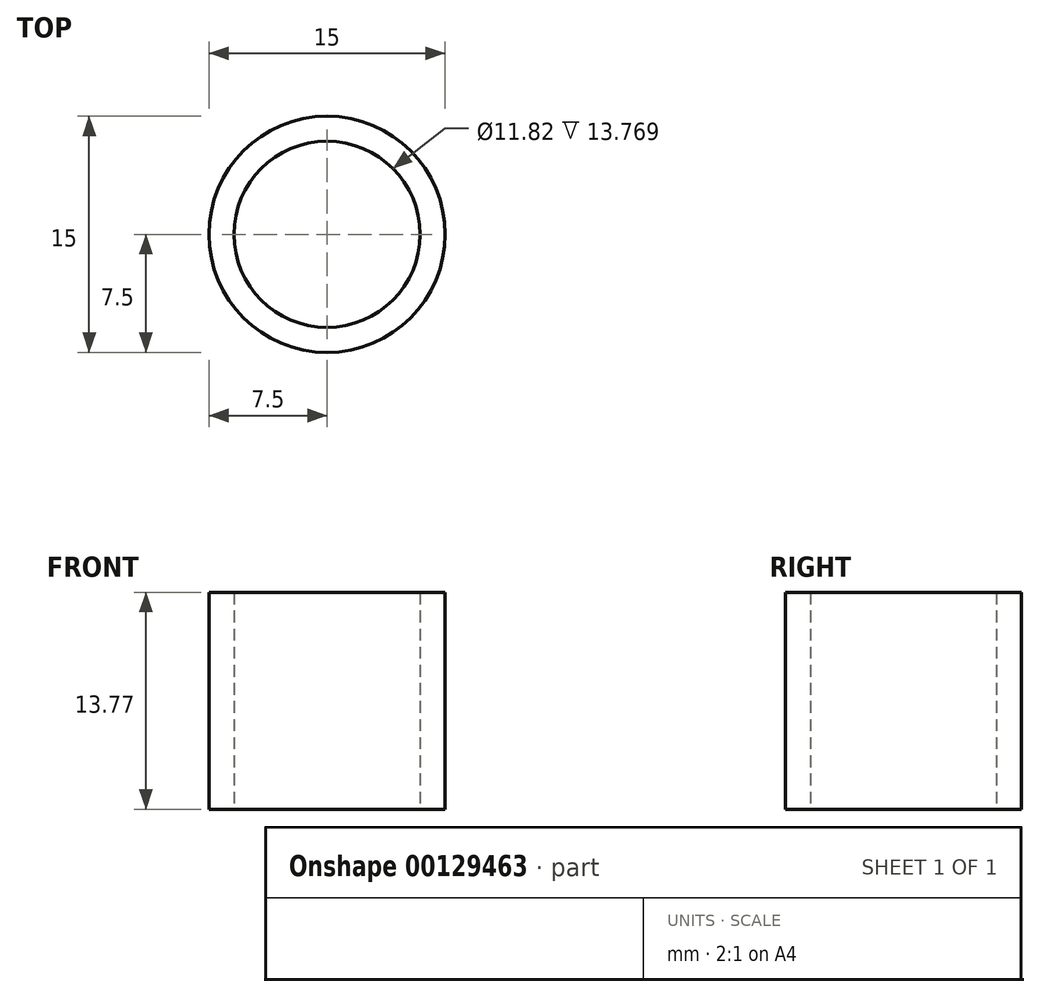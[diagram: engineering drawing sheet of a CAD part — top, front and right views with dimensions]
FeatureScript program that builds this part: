
annotation { "Feature Type Name" : "Feature", "Feature Type Description" : "" }
export const myFeature = defineFeature(function(context is Context, id is Id, definition is map)
    precondition{}
    {
        {
            var Q0;
            Q0=qCreatedBy(makeId("Top.planeOp"),FACE);
            var sketch = newSketch(context, id + "F0", { "sketchPlane" : qUnion([Q0])});
            skCircle(sketch, "E0", {"center": v(0, 0) * mm, "radius": 7.5 * mm});
            skCircle(sketch, "E1", {"center": v(0, 0) * mm, "radius": 5.91 * mm});
            skSolve(sketch);
        }
        {
            var Q0;
            Q0=qSketchRegion(id+"F0",true);
            extrude(context, id + "F1", {"entities" : qUnion([Q0]), "depth" : 13.77 * mm});
        }
    });
